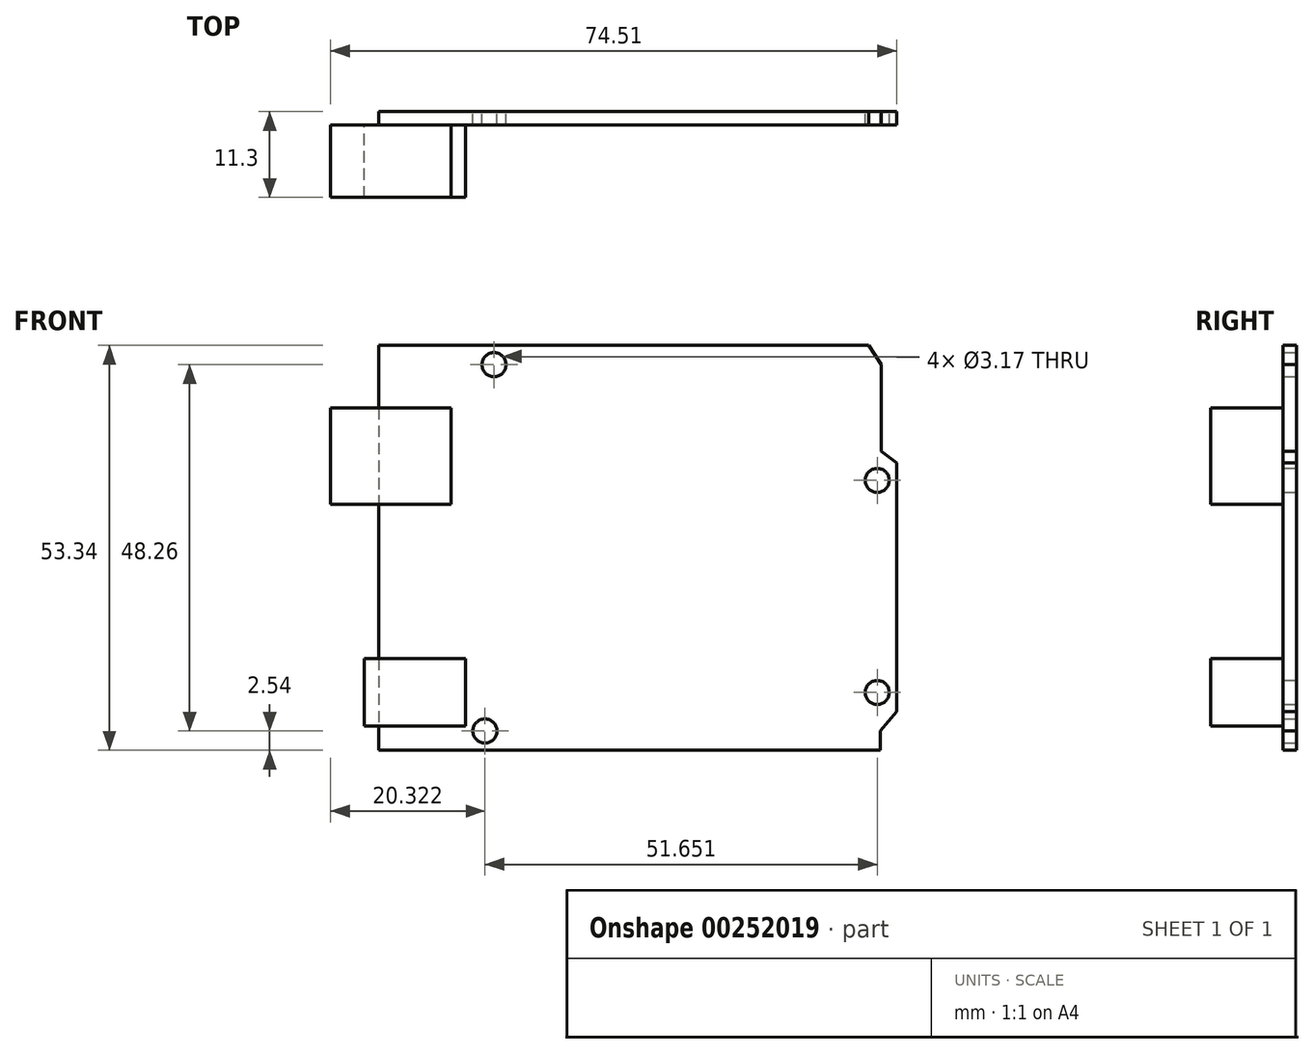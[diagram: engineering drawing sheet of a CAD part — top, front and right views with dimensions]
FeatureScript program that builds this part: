
annotation { "Feature Type Name" : "Feature", "Feature Type Description" : "" }
export const myFeature = defineFeature(function(context is Context, id is Id, definition is map)
    precondition{}
    {
        {
            var Q0;
            Q0=qCreatedBy(makeId("Front.planeOp"),FACE);
            var sketch = newSketch(context, id + "F0", { "sketchPlane" : qUnion([Q0])});
            skLineSegment(sketch, "E0", {"start": v(-39.3, 50.8) * mm, "end": v(-39.3, -2.54) * mm});
            skLineSegment(sketch, "E1", {"start": v(-39.3, -2.54) * mm, "end": v(26.74, -2.54) * mm});
            skLineSegment(sketch, "E2", {"start": v(-39.3, 50.8) * mm, "end": v(25.22, 50.8) * mm});
            skLineSegment(sketch, "E3", {"start": v(26.74, -2.54) * mm, "end": v(26.74, 0) * mm});
            skLineSegment(sketch, "E4", {"start": v(26.74, 0) * mm, "end": v(28.86, 2.54) * mm});
            skPoint(sketch, "E5.end.orphan", {"position": v(28.86, -2.54) * mm});
            skLineSegment(sketch, "E6", {"start": v(28.86, 2.54) * mm, "end": v(28.86, 35.3) * mm});
            skLineSegment(sketch, "E7", {"start": v(28.86, 35.3) * mm, "end": v(26.84, 36.84) * mm});
            skLineSegment(sketch, "E8", {"start": v(26.84, 36.84) * mm, "end": v(26.84, 48.27) * mm});
            skLineSegment(sketch, "E9", {"start": v(25.22, 50.8) * mm, "end": v(26.84, 48.27) * mm});
            skCircle(sketch, "E10", {"center": v(-25.33, 0) * mm, "radius": 1.59 * mm});
            skPoint(sketch, "E11.orphan", {"position": v(-39.3, 0) * mm});
            skCircle(sketch, "E12", {"center": v(-24.13, 48.26) * mm, "radius": 1.59 * mm});
            skCircle(sketch, "E13", {"center": v(26.32, 5.07) * mm, "radius": 1.59 * mm});
            skCircle(sketch, "E14", {"center": v(26.32, 33.01) * mm, "radius": 1.59 * mm});
            skSolve(sketch);
        }
        {
            var Q0;
            Q0=makeQuery(id+"F0.imprint","IMPRINT",FACE,{"disambiguationData":[TD([[makeQuery(id+"F0.imprint","IMPRINT",EDGE,{"derivedFrom":sQuery(id+"F0.wireOp",EDGE,"E0")}),1.0]])]});
            extrude(context, id + "F1", {"entities" : qUnion([Q0]), "depth" : 1.78 * mm});
        }
        {
            var Q0;
            Q0=makeQuery(id+"F1.opExtrude","CAP_FACE",FACE,{"disambiguationData":[OSD([sQuery(id+"F0.wireOp",EDGE,"E0"),sQuery(id+"F0.wireOp",EDGE,"E1"),sQuery(id+"F0.wireOp",EDGE,"E2"),sQuery(id+"F0.wireOp",EDGE,"E3"),sQuery(id+"F0.wireOp",EDGE,"E4"),sQuery(id+"F0.wireOp",EDGE,"E6"),sQuery(id+"F0.wireOp",EDGE,"E7"),sQuery(id+"F0.wireOp",EDGE,"E8"),sQuery(id+"F0.wireOp",EDGE,"E9"),sQuery(id+"F0.wireOp",EDGE,"E10"),sQuery(id+"F0.wireOp",EDGE,"E12"),sQuery(id+"F0.wireOp",EDGE,"E13"),sQuery(id+"F0.wireOp",EDGE,"E14")])],"isStart":false});
            var sketch = newSketch(context, id + "F2", { "sketchPlane" : qUnion([Q0])});
            skLineSegment(sketch, "E15", {"start": v(-27.87, 0.64) * mm, "end": v(-41.2, 0.64) * mm});
            skLineSegment(sketch, "E16", {"start": v(-41.2, 0.64) * mm, "end": v(-41.2, 9.53) * mm});
            skLineSegment(sketch, "E17", {"start": v(-41.2, 9.53) * mm, "end": v(-27.87, 9.53) * mm});
            skLineSegment(sketch, "E18", {"start": v(-27.87, 9.53) * mm, "end": v(-27.87, 0.64) * mm});
            skLineSegment(sketch, "E19", {"start": v(-29.77, 29.84) * mm, "end": v(-45.65, 29.84) * mm});
            skLineSegment(sketch, "E20", {"start": v(-45.65, 29.84) * mm, "end": v(-45.65, 42.55) * mm});
            skLineSegment(sketch, "E21", {"start": v(-45.65, 42.55) * mm, "end": v(-29.77, 42.55) * mm});
            skLineSegment(sketch, "E22", {"start": v(-29.77, 42.55) * mm, "end": v(-29.77, 29.84) * mm});
            skSolve(sketch);
        }
        {
            var Q0;
            {var subQ0=sQuery(id+"F2.wireOp",EDGE,"E22");Q0=makeQuery(id+"F2.imprint","IMPRINT",FACE,{"disambiguationData":[TD([[makeQuery(id+"F2.imprint","IMPRINT",EDGE,{"derivedFrom":subQ0}),-1.0]])]});}
            var Q1;
            {var subQ0=sQuery(id+"F2.wireOp",EDGE,"E20");Q1=makeQuery(id+"F2.imprint","IMPRINT",FACE,{"disambiguationData":[TD([[makeQuery(id+"F2.imprint","IMPRINT",EDGE,{"derivedFrom":subQ0}),-1.0]])]});}
            extrude(context, id + "F3", {"entities" : qUnion([Q0, Q1]), "operationType" : NewBodyOperationType.ADD, "depth" : 9.52 * mm});
        }
        {
            var Q0;
            {var subQ0=sQuery(id+"F2.wireOp",EDGE,"E16");Q0=makeQuery(id+"F2.imprint","IMPRINT",FACE,{"disambiguationData":[TD([[makeQuery(id+"F2.imprint","IMPRINT",EDGE,{"derivedFrom":subQ0}),-1.0]])]});}
            var Q1;
            {var subQ0=sQuery(id+"F2.wireOp",EDGE,"E18");Q1=makeQuery(id+"F2.imprint","IMPRINT",FACE,{"disambiguationData":[TD([[makeQuery(id+"F2.imprint","IMPRINT",EDGE,{"derivedFrom":subQ0}),-1.0]])]});}
            extrude(context, id + "F4", {"entities" : qUnion([Q0, Q1]), "operationType" : NewBodyOperationType.ADD, "depth" : 9.52 * mm});
        }
    });
